# Revit family: Serene_T&T_Window_E_Standard
name_source: partatom
category: Windows
revit_build: Autodesk Revit 2014 (Build: 20130308_1515(x64)
units: mm (PartAtom-declared; Revit-internal decimal feet)

## types (18) — shared parameters
Area Glazing Sash = 0.43 m²
Centered In Wall = Yes
Custom Sash Height = 1122 mm
Custom Sash Width = 522 mm  [stored 1.7126 ft]
DG Gasket Finish = Double Glazing Gasket Material
DG Gasket Tickness = 12 mm  [stored 0.0393701 ft]
DG Thickness Calc = 4 mm  [stored 0.0131234 ft]
Default Sill Height = 800 mm  [stored 2.62467 ft]
Description = Tilt and turn, Type E
Fixed Panel Left Width = 510 mm
Frame Thickness = 52 mm
Frame Width = 62 mm  [stored 0.203412 ft]
Length Transom = 510 mm
Limit Fixed Panel Height Max = 1800 mm  [stored 5.90551 ft]
Limit Fixed Panel Height Min = 200 mm  [stored 0.656168 ft]
Limit Fixed Panel Width Max = 1800 mm  [stored 5.90551 ft]
Limit Fixed Panel Width Min = 200 mm  [stored 0.656168 ft]
Limit Sash Height Max = 1500 mm  [stored 4.92126 ft]
Limit Sash Height Min = 300 mm  [stored 0.984252 ft]
Limit Sash Width Max = 700 mm  [stored 2.29659 ft]
Limit Sash Width Min = 300 mm  [stored 0.984252 ft]
Limit Window Height Max = 1880 mm  [stored 6.16798 ft]
Limit Window Height Min = 1430 mm
Limit Window Width Max = 2430 mm
Limit Window Width Min = 830 mm  [stored 2.7231 ft]
Manufacturer = Crealco
Max System DG One Piece Thickness = 4 mm  [stored 0.0131234 ft]
Max System DG Unit Thickness = 20 mm  [stored 0.0656168 ft]
Model = Serene
Sash Edge Gap = 34 mm
Sash Frame Gasket = 3 mm  [stored 0.00984252 ft]
Sash Height = 1122 mm
Sash Overlap = 28 mm  [stored 0.0918635 ft]
Sash Width = 522 mm  [stored 1.7126 ft]
URL = http://www.crealco.co.za
Wall Closure = By host
zero-valued in all types: Custom Window Exterior Offset

## per-type parameters (varying)
- 52TT-0915S-1000Pa: Area Glazing Fixed Panel Left=0.13 m²; Area Glazing Fixed Panel Right=0.35 m²; Clearvue Insulated LowE SHGC Value=0.397; Clearvue Insulated LowE U Value=4.11; Clearvue Insulated SHGC Value=0.435; Clearvue Insulated U Value=4.5; Clearvue SHGC Value=0.494; Clearvue U Value=6.24; Custom Windload=1000 mm  [stored 3.28084 ft]; Custom Window Height=1490 mm  [stored 4.88845 ft]; Custom Window Width=890 mm  [stored 2.91995 ft]; Energy Advantage SHGC Value=0.444; Energy Advantage U Value=5.64; Fixed Panel Left Height=260 mm; Fixed Panel Right Height=1410 mm  [stored 4.62598 ft]; Fixed Panel Right Width=260 mm; Heavy Duty Mullion=No; Height=1490 mm  [stored 4.88845 ft]; Intruderprufe LowE SHGC Value=0.406; Intruderprufe LowE U Value=4.58; Intruderprufe SHGC Value=0.458; Intruderprufe U Value=6.16; Length Decorative Mullion=1490 mm  [stored 4.88845 ft]; Length Mullion=1410 mm  [stored 4.62598 ft]; Max Pane Area=0.43 m²; Standard Mullion=Yes; Width=890 mm  [stored 2.91995 ft]; Windload Design=1000 mm  [stored 3.28084 ft]
- 52TT-0915S-1500Pa: Area Glazing Fixed Panel Left=0.13 m²; Area Glazing Fixed Panel Right=0.35 m²; Clearvue Insulated LowE SHGC Value=0.397; Clearvue Insulated LowE U Value=4.11; Clearvue Insulated SHGC Value=0.435; Clearvue Insulated U Value=4.5; Clearvue SHGC Value=0.494; Clearvue U Value=6.24; Custom Windload=1500 mm  [stored 4.92126 ft]; Custom Window Height=1490 mm  [stored 4.88845 ft]; Custom Window Width=890 mm  [stored 2.91995 ft]; Energy Advantage SHGC Value=0.444; Energy Advantage U Value=5.64; Fixed Panel Left Height=260 mm; Fixed Panel Right Height=1410 mm  [stored 4.62598 ft]; Fixed Panel Right Width=260 mm; Heavy Duty Mullion=No; Height=1490 mm  [stored 4.88845 ft]; Intruderprufe LowE SHGC Value=0.406; Intruderprufe LowE U Value=4.58; Intruderprufe SHGC Value=0.458; Intruderprufe U Value=6.16; Length Decorative Mullion=1490 mm  [stored 4.88845 ft]; Length Mullion=1410 mm  [stored 4.62598 ft]; Max Pane Area=0.43 m²; Standard Mullion=Yes; Width=890 mm  [stored 2.91995 ft]; Windload Design=1500 mm  [stored 4.92126 ft]
- 52TT-0915S-2000Pa: Area Glazing Fixed Panel Left=0.13 m²; Area Glazing Fixed Panel Right=0.35 m²; Clearvue Insulated LowE SHGC Value=0.397; Clearvue Insulated LowE U Value=4.11; Clearvue Insulated SHGC Value=0.435; Clearvue Insulated U Value=4.5; Clearvue SHGC Value=0.494; Clearvue U Value=6.24; Custom Windload=2000 mm  [stored 6.56168 ft]; Custom Window Height=1490 mm  [stored 4.88845 ft]; Custom Window Width=890 mm  [stored 2.91995 ft]; Energy Advantage SHGC Value=0.444; Energy Advantage U Value=5.64; Fixed Panel Left Height=260 mm; Fixed Panel Right Height=1410 mm  [stored 4.62598 ft]; Fixed Panel Right Width=260 mm; Heavy Duty Mullion=No; Height=1490 mm  [stored 4.88845 ft]; Intruderprufe LowE SHGC Value=0.406; Intruderprufe LowE U Value=4.58; Intruderprufe SHGC Value=0.458; Intruderprufe U Value=6.16; Length Decorative Mullion=1490 mm  [stored 4.88845 ft]; Length Mullion=1410 mm  [stored 4.62598 ft]; Max Pane Area=0.43 m²; Standard Mullion=Yes; Width=890 mm  [stored 2.91995 ft]; Windload Design=2000 mm  [stored 6.56168 ft]
- 52TT-1215S-1000Pa: Area Glazing Fixed Panel Left=0.13 m²; Area Glazing Fixed Panel Right=0.77 m²; Clearvue Insulated LowE SHGC Value=0.454; Clearvue Insulated LowE U Value=3.67; Clearvue Insulated SHGC Value=0.498; Clearvue Insulated U Value=4.14; Clearvue SHGC Value=0.566; Clearvue U Value=6.16; Custom Windload=1000 mm  [stored 3.28084 ft]; Custom Window Height=1490 mm  [stored 4.88845 ft]; Custom Window Width=1190 mm  [stored 3.9042 ft]; Energy Advantage SHGC Value=0.507; Energy Advantage U Value=5.26; Fixed Panel Left Height=260 mm; Fixed Panel Right Height=1410 mm  [stored 4.62598 ft]; Fixed Panel Right Width=560 mm; Heavy Duty Mullion=No; Height=1490 mm  [stored 4.88845 ft]; Intruderprufe LowE SHGC Value=0.464; Intruderprufe LowE U Value=4.5; Intruderprufe SHGC Value=0.523; Intruderprufe U Value=6.05; Length Decorative Mullion=1490 mm  [stored 4.88845 ft]; Length Mullion=1410 mm  [stored 4.62598 ft]; Max Pane Area=0.77 m²; Standard Mullion=Yes; Width=1190 mm  [stored 3.9042 ft]; Windload Design=1000 mm  [stored 3.28084 ft]
- 52TT-1215S-1500Pa: Area Glazing Fixed Panel Left=0.13 m²; Area Glazing Fixed Panel Right=0.77 m²; Clearvue Insulated LowE SHGC Value=0.454; Clearvue Insulated LowE U Value=3.67; Clearvue Insulated SHGC Value=0.498; Clearvue Insulated U Value=4.14; Clearvue SHGC Value=0.566; Clearvue U Value=6.16; Custom Windload=1500 mm  [stored 4.92126 ft]; Custom Window Height=1490 mm  [stored 4.88845 ft]; Custom Window Width=1190 mm  [stored 3.9042 ft]; Energy Advantage SHGC Value=0.507; Energy Advantage U Value=5.26; Fixed Panel Left Height=260 mm; Fixed Panel Right Height=1410 mm  [stored 4.62598 ft]; Fixed Panel Right Width=560 mm; Heavy Duty Mullion=No; Height=1490 mm  [stored 4.88845 ft]; Intruderprufe LowE SHGC Value=0.464; Intruderprufe LowE U Value=4.5; Intruderprufe SHGC Value=0.523; Intruderprufe U Value=6.05; Length Decorative Mullion=1490 mm  [stored 4.88845 ft]; Length Mullion=1410 mm  [stored 4.62598 ft]; Max Pane Area=0.77 m²; Standard Mullion=Yes; Width=1190 mm  [stored 3.9042 ft]; Windload Design=1500 mm  [stored 4.92126 ft]
- 52TT-1215S-2000Pa: Area Glazing Fixed Panel Left=0.13 m²; Area Glazing Fixed Panel Right=0.77 m²; Clearvue Insulated LowE SHGC Value=0.454; Clearvue Insulated LowE U Value=3.67; Clearvue Insulated SHGC Value=0.498; Clearvue Insulated U Value=4.14; Clearvue SHGC Value=0.566; Clearvue U Value=6.16; Custom Windload=2000 mm  [stored 6.56168 ft]; Custom Window Height=1490 mm  [stored 4.88845 ft]; Custom Window Width=1190 mm  [stored 3.9042 ft]; Energy Advantage SHGC Value=0.507; Energy Advantage U Value=5.26; Fixed Panel Left Height=260 mm; Fixed Panel Right Height=1410 mm  [stored 4.62598 ft]; Fixed Panel Right Width=560 mm; Heavy Duty Mullion=Yes; Height=1490 mm  [stored 4.88845 ft]; Intruderprufe LowE SHGC Value=0.464; Intruderprufe LowE U Value=4.5; Intruderprufe SHGC Value=0.523; Intruderprufe U Value=6.05; Length Decorative Mullion=1490 mm  [stored 4.88845 ft]; Length Mullion=1410 mm  [stored 4.62598 ft]; Max Pane Area=0.77 m²; Standard Mullion=No; Width=1190 mm  [stored 3.9042 ft]; Windload Design=2000 mm  [stored 6.56168 ft]
- 52TT-1515S-1000Pa: Area Glazing Fixed Panel Left=0.13 m²; Area Glazing Fixed Panel Right=1.19 m²; Clearvue Insulated LowE SHGC Value=0.488; Clearvue Insulated LowE U Value=3.4; Clearvue Insulated SHGC Value=0.536; Clearvue Insulated U Value=3.93; Clearvue SHGC Value=0.609; Clearvue U Value=6.11; Custom Windload=1000 mm  [stored 3.28084 ft]; Custom Window Height=1490 mm  [stored 4.88845 ft]; Custom Window Width=1490 mm  [stored 4.88845 ft]; Energy Advantage SHGC Value=0.545; Energy Advantage U Value=5.04; Fixed Panel Left Height=260 mm; Fixed Panel Right Height=1410 mm  [stored 4.62598 ft]; Fixed Panel Right Width=860 mm  [stored 2.82152 ft]; Heavy Duty Mullion=No; Height=1490 mm  [stored 4.88845 ft]; Intruderprufe LowE SHGC Value=0.499; Intruderprufe LowE U Value=4.45; Intruderprufe SHGC Value=0.563; Intruderprufe U Value=5.98; Length Decorative Mullion=1490 mm  [stored 4.88845 ft]; Length Mullion=1410 mm  [stored 4.62598 ft]; Max Pane Area=1.19 m²; Standard Mullion=Yes; Width=1490 mm  [stored 4.88845 ft]; Windload Design=1000 mm  [stored 3.28084 ft]
- 52TT-1515S-1500Pa: Area Glazing Fixed Panel Left=0.13 m²; Area Glazing Fixed Panel Right=1.19 m²; Clearvue Insulated LowE SHGC Value=0.488; Clearvue Insulated LowE U Value=3.4; Clearvue Insulated SHGC Value=0.536; Clearvue Insulated U Value=3.93; Clearvue SHGC Value=0.609; Clearvue U Value=6.11; Custom Windload=1500 mm  [stored 4.92126 ft]; Custom Window Height=1490 mm  [stored 4.88845 ft]; Custom Window Width=1490 mm  [stored 4.88845 ft]; Energy Advantage SHGC Value=0.545; Energy Advantage U Value=5.04; Fixed Panel Left Height=260 mm; Fixed Panel Right Height=1410 mm  [stored 4.62598 ft]; Fixed Panel Right Width=860 mm  [stored 2.82152 ft]; Heavy Duty Mullion=Yes; Height=1490 mm  [stored 4.88845 ft]; Intruderprufe LowE SHGC Value=0.499; Intruderprufe LowE U Value=4.45; Intruderprufe SHGC Value=0.563; Intruderprufe U Value=5.98; Length Decorative Mullion=1490 mm  [stored 4.88845 ft]; Length Mullion=1410 mm  [stored 4.62598 ft]; Max Pane Area=1.19 m²; Standard Mullion=No; Width=1490 mm  [stored 4.88845 ft]; Windload Design=1500 mm  [stored 4.92126 ft]
- 52TT-1515S-2000Pa: Area Glazing Fixed Panel Left=0.13 m²; Area Glazing Fixed Panel Right=1.19 m²; Clearvue Insulated LowE SHGC Value=0.488; Clearvue Insulated LowE U Value=3.4; Clearvue Insulated SHGC Value=0.536; Clearvue Insulated U Value=3.93; Clearvue SHGC Value=0.609; Clearvue U Value=6.11; Custom Windload=2000 mm  [stored 6.56168 ft]; Custom Window Height=1490 mm  [stored 4.88845 ft]; Custom Window Width=1490 mm  [stored 4.88845 ft]; Energy Advantage SHGC Value=0.545; Energy Advantage U Value=5.04; Fixed Panel Left Height=260 mm; Fixed Panel Right Height=1410 mm  [stored 4.62598 ft]; Fixed Panel Right Width=860 mm  [stored 2.82152 ft]; Heavy Duty Mullion=Yes; Height=1490 mm  [stored 4.88845 ft]; Intruderprufe LowE SHGC Value=0.499; Intruderprufe LowE U Value=4.45; Intruderprufe SHGC Value=0.563; Intruderprufe U Value=5.98; Length Decorative Mullion=1490 mm  [stored 4.88845 ft]; Length Mullion=1410 mm  [stored 4.62598 ft]; Max Pane Area=1.19 m²; Standard Mullion=No; Width=1490 mm  [stored 4.88845 ft]; Windload Design=2000 mm  [stored 6.56168 ft]
- 52TT-0918S-1000Pa: Area Glazing Fixed Panel Left=0.27 m²; Area Glazing Fixed Panel Right=0.43 m²; Clearvue Insulated LowE SHGC Value=0.414; Clearvue Insulated LowE U Value=3.98; Clearvue Insulated SHGC Value=0.454; Clearvue Insulated U Value=4.39; Clearvue SHGC Value=0.516; Clearvue U Value=6.2; Custom Windload=1000 mm  [stored 3.28084 ft]; Custom Window Height=1790 mm  [stored 5.8727 ft]; Custom Window Width=890 mm  [stored 2.91995 ft]; Energy Advantage SHGC Value=0.464; Energy Advantage U Value=5.55; Fixed Panel Left Height=560 mm; Fixed Panel Right Height=1710 mm  [stored 5.61024 ft]; Fixed Panel Right Width=260 mm; Heavy Duty Mullion=No; Height=1790 mm  [stored 5.8727 ft]; Intruderprufe LowE SHGC Value=0.424; Intruderprufe LowE U Value=4.55; Intruderprufe SHGC Value=0.478; Intruderprufe U Value=6.12; Length Decorative Mullion=1790 mm  [stored 5.8727 ft]; Length Mullion=1710 mm  [stored 5.61024 ft]; Max Pane Area=0.43 m²; Standard Mullion=Yes; Width=890 mm  [stored 2.91995 ft]; Windload Design=1000 mm  [stored 3.28084 ft]
- 52TT-0918S-1500Pa: Area Glazing Fixed Panel Left=0.27 m²; Area Glazing Fixed Panel Right=0.43 m²; Clearvue Insulated LowE SHGC Value=0.414; Clearvue Insulated LowE U Value=3.98; Clearvue Insulated SHGC Value=0.454; Clearvue Insulated U Value=4.39; Clearvue SHGC Value=0.516; Clearvue U Value=6.2; Custom Windload=1500 mm  [stored 4.92126 ft]; Custom Window Height=1790 mm  [stored 5.8727 ft]; Custom Window Width=890 mm  [stored 2.91995 ft]; Energy Advantage SHGC Value=0.464; Energy Advantage U Value=5.55; Fixed Panel Left Height=560 mm; Fixed Panel Right Height=1710 mm  [stored 5.61024 ft]; Fixed Panel Right Width=260 mm; Heavy Duty Mullion=Yes; Height=1790 mm  [stored 5.8727 ft]; Intruderprufe LowE SHGC Value=0.424; Intruderprufe LowE U Value=4.55; Intruderprufe SHGC Value=0.478; Intruderprufe U Value=6.12; Length Decorative Mullion=1790 mm  [stored 5.8727 ft]; Length Mullion=1710 mm  [stored 5.61024 ft]; Max Pane Area=0.43 m²; Standard Mullion=No; Width=890 mm  [stored 2.91995 ft]; Windload Design=1500 mm  [stored 4.92126 ft]
- 52TT-0918S-2000Pa: Area Glazing Fixed Panel Left=0.27 m²; Area Glazing Fixed Panel Right=0.43 m²; Clearvue Insulated LowE SHGC Value=0.414; Clearvue Insulated LowE U Value=3.98; Clearvue Insulated SHGC Value=0.454; Clearvue Insulated U Value=4.39; Clearvue SHGC Value=0.516; Clearvue U Value=6.2; Custom Windload=2000 mm  [stored 6.56168 ft]; Custom Window Height=1790 mm  [stored 5.8727 ft]; Custom Window Width=890 mm  [stored 2.91995 ft]; Energy Advantage SHGC Value=0.464; Energy Advantage U Value=5.55; Fixed Panel Left Height=560 mm; Fixed Panel Right Height=1710 mm  [stored 5.61024 ft]; Fixed Panel Right Width=260 mm; Heavy Duty Mullion=Yes; Height=1790 mm  [stored 5.8727 ft]; Intruderprufe LowE SHGC Value=0.424; Intruderprufe LowE U Value=4.55; Intruderprufe SHGC Value=0.478; Intruderprufe U Value=6.12; Length Decorative Mullion=1790 mm  [stored 5.8727 ft]; Length Mullion=1710 mm  [stored 5.61024 ft]; Max Pane Area=0.43 m²; Standard Mullion=No; Width=890 mm  [stored 2.91995 ft]; Windload Design=2000 mm  [stored 6.56168 ft]
- 52TT-1218S-1000Pa: Area Glazing Fixed Panel Left=0.27 m²; Area Glazing Fixed Panel Right=0.94 m²; Clearvue Insulated LowE SHGC Value=0.469; Clearvue Insulated LowE U Value=3.55; Clearvue Insulated SHGC Value=0.515; Clearvue Insulated U Value=4.04; Clearvue SHGC Value=0.586; Clearvue U Value=6.13; Custom Windload=1000 mm  [stored 3.28084 ft]; Custom Window Height=1790 mm  [stored 5.8727 ft]; Custom Window Width=1190 mm  [stored 3.9042 ft]; Energy Advantage SHGC Value=0.525; Energy Advantage U Value=5.17; Fixed Panel Left Height=560 mm; Fixed Panel Right Height=1710 mm  [stored 5.61024 ft]; Fixed Panel Right Width=560 mm; Heavy Duty Mullion=Yes; Height=1790 mm  [stored 5.8727 ft]; Intruderprufe LowE SHGC Value=0.48; Intruderprufe LowE U Value=4.47; Intruderprufe SHGC Value=0.542; Intruderprufe U Value=6.01; Length Decorative Mullion=1790 mm  [stored 5.8727 ft]; Length Mullion=1710 mm  [stored 5.61024 ft]; Max Pane Area=0.94 m²; Standard Mullion=No; Width=1190 mm  [stored 3.9042 ft]; Windload Design=1000 mm  [stored 3.28084 ft]
- 52TT-1218S-1500Pa: Area Glazing Fixed Panel Left=0.27 m²; Area Glazing Fixed Panel Right=0.94 m²; Clearvue Insulated LowE SHGC Value=0.469; Clearvue Insulated LowE U Value=3.55; Clearvue Insulated SHGC Value=0.515; Clearvue Insulated U Value=4.04; Clearvue SHGC Value=0.586; Clearvue U Value=6.13; Custom Windload=1500 mm  [stored 4.92126 ft]; Custom Window Height=1790 mm  [stored 5.8727 ft]; Custom Window Width=1190 mm  [stored 3.9042 ft]; Energy Advantage SHGC Value=0.525; Energy Advantage U Value=5.17; Fixed Panel Left Height=560 mm; Fixed Panel Right Height=1710 mm  [stored 5.61024 ft]; Fixed Panel Right Width=560 mm; Heavy Duty Mullion=Yes; Height=1790 mm  [stored 5.8727 ft]; Intruderprufe LowE SHGC Value=0.48; Intruderprufe LowE U Value=4.47; Intruderprufe SHGC Value=0.542; Intruderprufe U Value=6.01; Length Decorative Mullion=1790 mm  [stored 5.8727 ft]; Length Mullion=1710 mm  [stored 5.61024 ft]; Max Pane Area=0.94 m²; Standard Mullion=No; Width=1190 mm  [stored 3.9042 ft]; Windload Design=1500 mm  [stored 4.92126 ft]
- 52TT-1218S-2000Pa: Area Glazing Fixed Panel Left=0.27 m²; Area Glazing Fixed Panel Right=0.94 m²; Clearvue Insulated LowE SHGC Value=0.469; Clearvue Insulated LowE U Value=3.55; Clearvue Insulated SHGC Value=0.515; Clearvue Insulated U Value=4.04; Clearvue SHGC Value=0.586; Clearvue U Value=6.13; Custom Windload=2000 mm  [stored 6.56168 ft]; Custom Window Height=1790 mm  [stored 5.8727 ft]; Custom Window Width=1190 mm  [stored 3.9042 ft]; Energy Advantage SHGC Value=0.525; Energy Advantage U Value=5.17; Fixed Panel Left Height=560 mm; Fixed Panel Right Height=1710 mm  [stored 5.61024 ft]; Fixed Panel Right Width=560 mm; Heavy Duty Mullion=Yes; Height=1790 mm  [stored 5.8727 ft]; Intruderprufe LowE SHGC Value=0.48; Intruderprufe LowE U Value=4.47; Intruderprufe SHGC Value=0.542; Intruderprufe U Value=6.01; Length Decorative Mullion=1790 mm  [stored 5.8727 ft]; Length Mullion=1710 mm  [stored 5.61024 ft]; Max Pane Area=0.94 m²; Standard Mullion=No; Width=1190 mm  [stored 3.9042 ft]; Windload Design=2000 mm  [stored 6.56168 ft]
- 52TT-1518S-1000Pa: Area Glazing Fixed Panel Left=0.27 m²; Area Glazing Fixed Panel Right=1.45 m²; Clearvue Insulated LowE SHGC Value=0.502; Clearvue Insulated LowE U Value=3.29; Clearvue Insulated SHGC Value=0.552; Clearvue Insulated U Value=3.84; Clearvue SHGC Value=0; Clearvue U Value=7.9; Custom Windload=1000 mm  [stored 3.28084 ft]; Custom Window Height=1790 mm  [stored 5.8727 ft]; Custom Window Width=1490 mm  [stored 4.88845 ft]; Energy Advantage SHGC Value=0; Energy Advantage U Value=7.9; Fixed Panel Left Height=560 mm; Fixed Panel Right Height=1710 mm  [stored 5.61024 ft]; Fixed Panel Right Width=860 mm  [stored 2.82152 ft]; Heavy Duty Mullion=Yes; Height=1790 mm  [stored 5.8727 ft]; Intruderprufe LowE SHGC Value=0.514; Intruderprufe LowE U Value=4.42; Intruderprufe SHGC Value=0.58; Intruderprufe U Value=5.95; Length Decorative Mullion=1790 mm  [stored 5.8727 ft]; Length Mullion=1710 mm  [stored 5.61024 ft]; Max Pane Area=1.45 m²; Standard Mullion=No; Width=1490 mm  [stored 4.88845 ft]; Windload Design=1000 mm  [stored 3.28084 ft]
- 52TT-1518S-1500Pa: Area Glazing Fixed Panel Left=0.27 m²; Area Glazing Fixed Panel Right=1.45 m²; Clearvue Insulated LowE SHGC Value=0.502; Clearvue Insulated LowE U Value=3.29; Clearvue Insulated SHGC Value=0.552; Clearvue Insulated U Value=3.84; Clearvue SHGC Value=0; Clearvue U Value=7.9; Custom Windload=1500 mm  [stored 4.92126 ft]; Custom Window Height=1790 mm  [stored 5.8727 ft]; Custom Window Width=1490 mm  [stored 4.88845 ft]; Energy Advantage SHGC Value=0; Energy Advantage U Value=7.9; Fixed Panel Left Height=560 mm; Fixed Panel Right Height=1710 mm  [stored 5.61024 ft]; Fixed Panel Right Width=860 mm  [stored 2.82152 ft]; Heavy Duty Mullion=Yes; Height=1790 mm  [stored 5.8727 ft]; Intruderprufe LowE SHGC Value=0.514; Intruderprufe LowE U Value=4.42; Intruderprufe SHGC Value=0.58; Intruderprufe U Value=5.95; Length Decorative Mullion=1790 mm  [stored 5.8727 ft]; Length Mullion=1710 mm  [stored 5.61024 ft]; Max Pane Area=1.45 m²; Standard Mullion=No; Width=1490 mm  [stored 4.88845 ft]; Windload Design=1500 mm  [stored 4.92126 ft]
- 52TT-1518S-2000Pa: Area Glazing Fixed Panel Left=0.27 m²; Area Glazing Fixed Panel Right=1.45 m²; Clearvue Insulated LowE SHGC Value=0.502; Clearvue Insulated LowE U Value=3.29; Clearvue Insulated SHGC Value=0.552; Clearvue Insulated U Value=3.84; Clearvue SHGC Value=0; Clearvue U Value=7.9; Custom Windload=2000 mm  [stored 6.56168 ft]; Custom Window Height=1790 mm  [stored 5.8727 ft]; Custom Window Width=1490 mm  [stored 4.88845 ft]; Energy Advantage SHGC Value=0; Energy Advantage U Value=7.9; Fixed Panel Left Height=560 mm; Fixed Panel Right Height=1710 mm  [stored 5.61024 ft]; Fixed Panel Right Width=860 mm  [stored 2.82152 ft]; Heavy Duty Mullion=Yes; Height=1790 mm  [stored 5.8727 ft]; Intruderprufe LowE SHGC Value=0.514; Intruderprufe LowE U Value=4.42; Intruderprufe SHGC Value=0.58; Intruderprufe U Value=5.95; Length Decorative Mullion=1790 mm  [stored 5.8727 ft]; Length Mullion=1710 mm  [stored 5.61024 ft]; Max Pane Area=1.45 m²; Standard Mullion=No; Width=1490 mm  [stored 4.88845 ft]; Windload Design=2000 mm  [stored 6.56168 ft]

note: [stored X ft] marks values corroborated as IEEE doubles in the binary element streams (Revit-internal decimal feet)

## geometry (parser evidence)
native form markers: Sweep x43
no freeform markers — native parametric forms only
